# Revit family: Control_Panels-Lutron-HomeWorks-PD4-36-F
name_source: partatom
category: Electrical Equipment
revit_build: Autodesk Revit 2017 (Build: 20160720_1515(x64)
units: mm (PartAtom-declared; Revit-internal decimal feet)

## family parameters
Cut with Voids When Loaded = No
Host = Face
OmniClass Number = 23.80.30.11.17
OmniClass Title = Distribution Boards and Control Panels
Panel Configuration = Two Columns, Circuits Across
Part Type = Panelboard
Room Calculation Point = No
Round Connector Dimension = Use Radius
Shared = No

## types (1)
- PD4-36-F
    Assembly Code = D5020
    Clearance Material = Clearance - Lutron - Transparent Red
    Cost = 0 $
    DIN Rail Quantity = 4
    Default Elevation = 6' - 6"
    Description = DIN Switching Panel
    Door Depth = 0' - 1 9/16"
    Electrical Potential = 0.00 V
    Enclosure Material = Steel - Lutron - Black
    Feed Through Control Circuit Voltage = 120.00 V
    Ground Bus = Yes
    Instruction Sheet Link = http://www.lutron.com
    Load Classification = Power
    MCB Rating = 0 A
    Manufacturer = Lutron Electronics Co., Inc
    Manufacturer Fax Number = 610-282-1243
    Maximum Feed Amps = 0 A
    Model = PD4-36-F
    Mounting Tab Center to Panel Top = 0' - 2 27/32"
    Mounting Tab Horizontal Center to Center = 1' - 1"
    Mounting Tab Radius = 0' - 0 5/8"
    Mounting Tab Thickness = 0' - 0 1/8"
    Mounting Tab Top to Panel Top = 0' - 2 7/32"
    Mounting Tab Vertical Center to Center = 1' - 11"
    Neutral Bus = Yes
    Neutral Rating = 0.00%
    Number of Poles = 3
    Overall Depth = 0' - 5 21/32"
    Overall Height = 3' - 0 21/32"
    Overall Width = 1' - 7 3/32"
    Panel Depth = 0' - 3 31/32"
    Panel Height = 3' - 0 1/4"
    Panel Thickness = 0' - 0 1/16"
    Panel Width = 1' - 5 29/32"
    Performance URL = http://www.lutron.com
    Phase = 1
    Product Documentation Link = http://www.lutron.com
    Product Name = DIN Switching Panel
    Product Page URL = http://www.lutron.com
    Rail Center to Rail Center = 0' - 5 1/2"
    Rail Inside Height = 0' - 1"
    Rail Left Offset = 0' - 4"
    Rail Length = 1' - 2"
    Rail Material = Steel - Lutron - Chrome Plated
    Rail Middle Offset from Right = 0' - 8 3/32"
    Rail Overall Depth = 0' - 0 5/16"
    Rail Overall Height = 0' - 1 3/8"
    Rail Right Offset = 0' - 1 3/32"
    Rail Thickness = 0' - 0 1/32"
    Recess Void Depth = 0' - 4 3/32"
    Series = HomeWorks® QS
    SubFeed Lugs = No
    Top Rail Center to Top = 0' - 7"
    URL = http://www.lutron.com
    Unit Weight = 0.00 lb
    Version = 2017 - v1.0b
    Video Link = https://www.youtube.com
    Voltage = 0.00 V
    Warranty URL = http://www.lutron.com

## geometry (parser evidence)
native form markers: Sweep x8
no freeform markers — native parametric forms only
